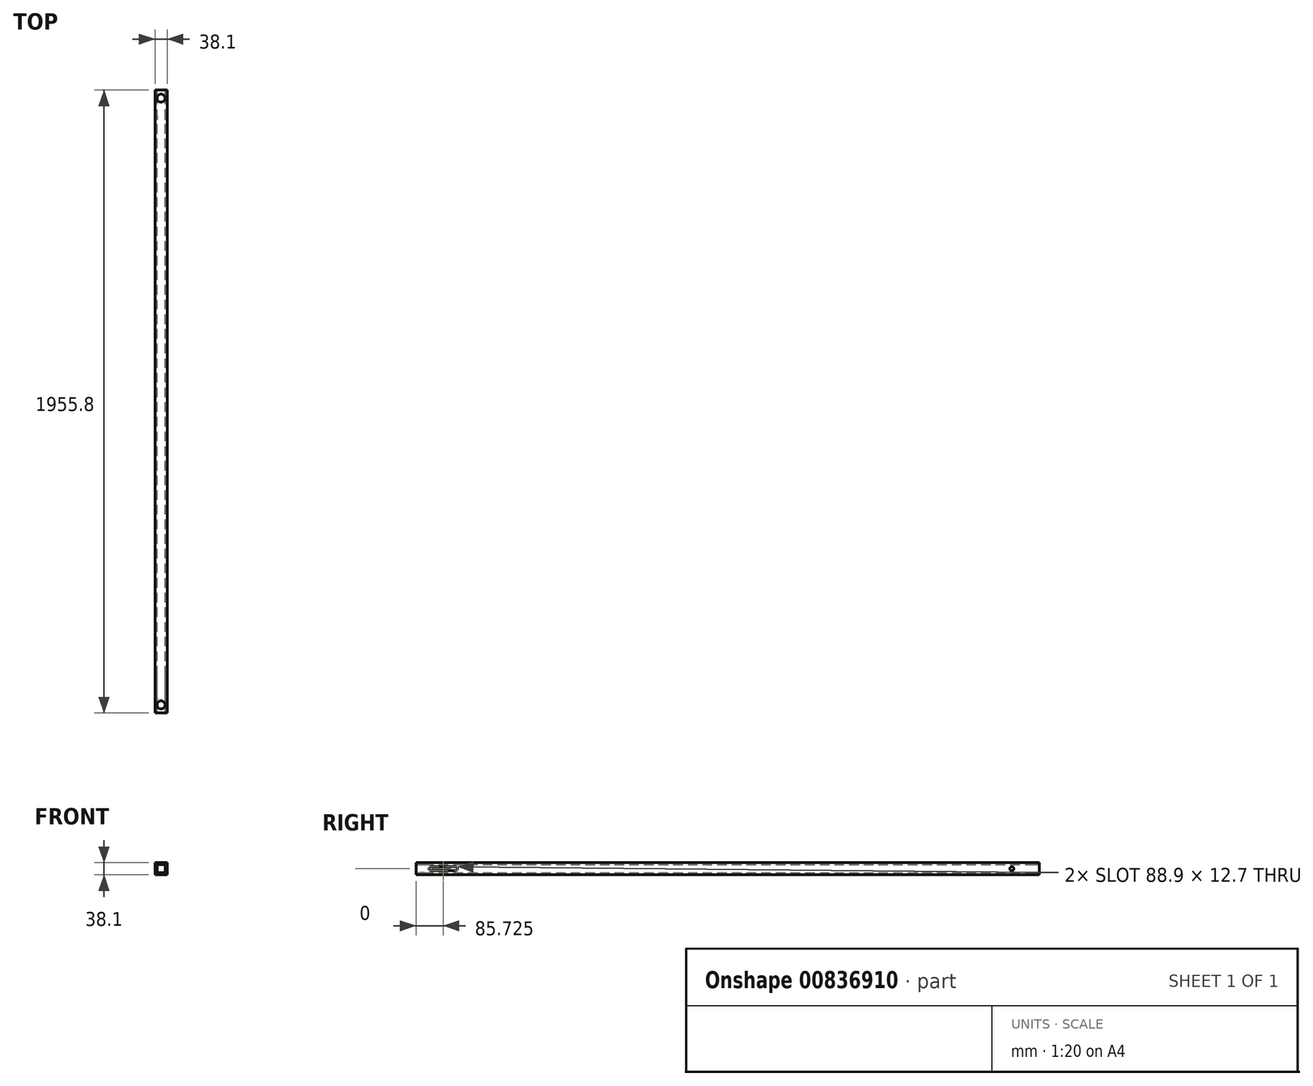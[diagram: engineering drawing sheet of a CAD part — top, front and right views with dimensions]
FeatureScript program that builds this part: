
annotation { "Feature Type Name" : "Feature", "Feature Type Description" : "" }
export const myFeature = defineFeature(function(context is Context, id is Id, definition is map)
    precondition{}
    {
        {
            var Q0;
            Q0=qCreatedBy(makeId("Front.planeOp"),FACE);
            var sketch = newSketch(context, id + "F0", { "sketchPlane" : qUnion([Q0])});
            skLineSegment(sketch, "E0.bottom", {"start": v(19.05, 19.05) * mm, "end": v(-19.05, 19.05) * mm});
            skLineSegment(sketch, "E0.top", {"start": v(19.05, -19.05) * mm, "end": v(-19.05, -19.05) * mm});
            skLineSegment(sketch, "E0.left", {"start": v(19.05, 19.05) * mm, "end": v(19.05, -19.05) * mm});
            skLineSegment(sketch, "E0.right", {"start": v(-19.05, 19.05) * mm, "end": v(-19.05, -19.05) * mm});
            skPoint(sketch, "E0.middle", {"position": v(0, 0) * mm});
            skLineSegment(sketch, "E1.bottom", {"start": v(-12.7, 12.7) * mm, "end": v(12.7, 12.7) * mm});
            skLineSegment(sketch, "E1.top", {"start": v(-12.7, -12.7) * mm, "end": v(12.7, -12.7) * mm});
            skLineSegment(sketch, "E1.left", {"start": v(-12.7, 12.7) * mm, "end": v(-12.7, -12.7) * mm});
            skLineSegment(sketch, "E1.right", {"start": v(12.7, 12.7) * mm, "end": v(12.7, -12.7) * mm});
            skSolve(sketch);
        }
        {
            var Q0;
            Q0=qSketchRegion(id+"F0",true);
            extrude(context, id + "F1", {"entities" : qUnion([Q0]), "depth" : 1955.8 * mm, "offsetDistance" : 25.4 * mm, "symmetric" : true});
        }
        {
            var Q0;
            Q0=qCreatedBy(makeId("Top.planeOp"),FACE);
            var sketch = newSketch(context, id + "F2", { "sketchPlane" : qUnion([Q0])});
            skCircle(sketch, "E2", {"center": v(0, -952.5) * mm, "radius": 12.7 * mm});
            skCircle(sketch, "E3", {"center": v(0, 952.5) * mm, "radius": 12.7 * mm});
            skSolve(sketch);
        }
        {
            var Q0;
            Q0 = qSketchRegion(id + "F2", true);
            extrude(context, id + "F3", {"entities" : qUnion([Q0]), "operationType" : NewBodyOperationType.REMOVE, "depth" : 635 * mm, "offsetDistance" : 25.4 * mm, "symmetric" : true});
        }
        {
            var Q0;
            Q0=makeQuery(id+"F1.opExtrude","SWEPT_FACE",FACE,{"disambiguationData":[OSD([sQuery(id+"F0.wireOp",EDGE,"E0.left")])]});
            var sketch = newSketch(context, id + "F4", { "sketchPlane" : qUnion([Q0])});
            skCircle(sketch, "E4", {"center": v(892.18, 0) * mm, "radius": 6.35 * mm});
            skSolve(sketch);
        }
        {
            var Q0;
            Q0 = qSketchRegion(id + "F4", true);
            extrude(context, id + "F5", {"entities" : qUnion([Q0]), "operationType" : NewBodyOperationType.REMOVE, "oppositeDirection" : true, "depth" : 76.2 * mm, "offsetDistance" : 25.4 * mm});
        }
        {
            var Q0;
            Q0=makeQuery(id+"F1.opExtrude","SWEPT_FACE",FACE,{"disambiguationData":[OSD([sQuery(id+"F0.wireOp",EDGE,"E0.left")])]});
            var sketch = newSketch(context, id + "F6", { "sketchPlane" : qUnion([Q0])});
            skLineSegment(sketch, "E5.bottom", {"start": v(-930.28, 6.35) * mm, "end": v(-854.08, 6.35) * mm});
            skLineSegment(sketch, "E5.top", {"start": v(-930.28, -6.35) * mm, "end": v(-854.08, -6.35) * mm});
            skPoint(sketch, "E5.middle", {"position": v(-892.18, 0) * mm});
            skPoint(sketch, "E5.middle.positionSnap0", {"position": v(-977.9, 0) * mm});
            skPoint(sketch, "E5.centerSnap0", {"position": v(-977.9, 0) * mm});
            skArc(sketch, "E6", {"start": v(-930.28, 6.35) * mm, "mid": v(-936.62, 0) * mm, "end": v(-930.28, -6.35) * mm});
            skArc(sketch, "E7", {"start": v(-854.08, -6.35) * mm, "mid": v(-847.73, 0) * mm, "end": v(-854.08, 6.35) * mm});
            skSolve(sketch);
        }
        {
            var Q0;
            Q0 = qSketchRegion(id + "F6", true);
            extrude(context, id + "F7", {"entities" : qUnion([Q0]), "operationType" : NewBodyOperationType.REMOVE, "oppositeDirection" : true, "depth" : 50.8 * mm, "offsetDistance" : 25.4 * mm});
        }
    });
